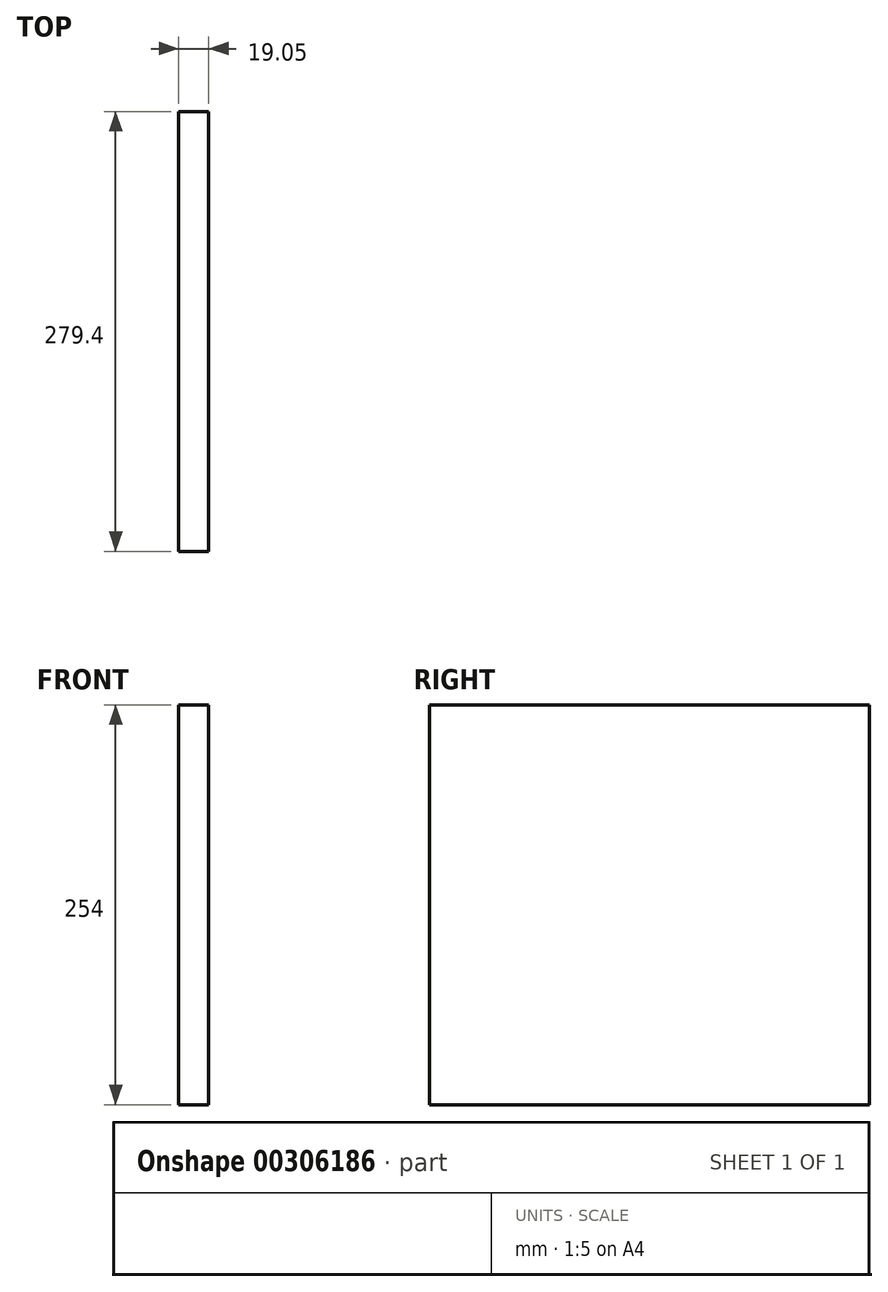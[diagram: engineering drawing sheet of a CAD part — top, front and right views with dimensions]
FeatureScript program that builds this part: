
annotation { "Feature Type Name" : "Feature", "Feature Type Description" : "" }
export const myFeature = defineFeature(function(context is Context, id is Id, definition is map)
    precondition{}
    {
        {
            var Q0;
            Q0=qCreatedBy(makeId("Right.planeOp"),FACE);
            var sketch = newSketch(context, id + "F0", { "sketchPlane" : qUnion([Q0])});
            skLineSegment(sketch, "E0.bottom", {"start": v(139.7, 127) * mm, "end": v(-139.7, 127) * mm});
            skLineSegment(sketch, "E0.top", {"start": v(139.7, -127) * mm, "end": v(-139.7, -127) * mm});
            skLineSegment(sketch, "E0.left", {"start": v(139.7, 127) * mm, "end": v(139.7, -127) * mm});
            skLineSegment(sketch, "E0.right", {"start": v(-139.7, 127) * mm, "end": v(-139.7, -127) * mm});
            skPoint(sketch, "E0.middle", {"position": v(0, 0) * mm});
            skSolve(sketch);
        }
        {
            var Q0;
            Q0=makeQuery(id+"F0.imprint","IMPRINT",FACE,{"disambiguationData":[TD([[makeQuery(id+"F0.imprint","IMPRINT",EDGE,{"derivedFrom":sQuery(id+"F0.wireOp",EDGE,"E0.bottom")}),1.0]])]});
            extrude(context, id + "F1", {"entities" : qUnion([Q0]), "depth" : 19.05 * mm});
        }
    });
